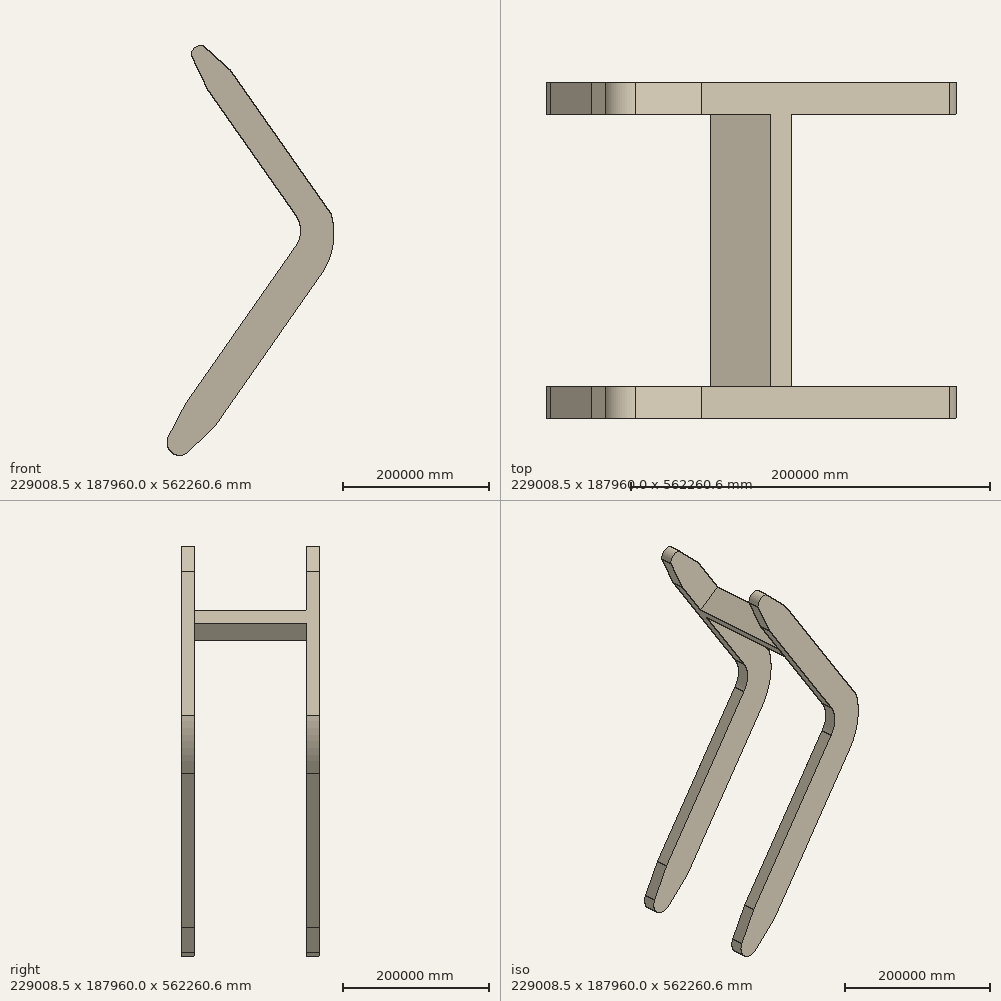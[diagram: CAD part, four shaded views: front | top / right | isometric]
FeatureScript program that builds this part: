
annotation { "Feature Type Name" : "Feature", "Feature Type Description" : "" }
export const myFeature = defineFeature(function(context is Context, id is Id, definition is map)
    precondition{}
    {
        {
            var Q0;
            Q0=qCreatedBy(makeId("Front.planeOp"),FACE);
            var sketch = newSketch(context, id + "F0", { "sketchPlane" : qUnion([Q0])});
            skLineSegment(sketch, "E0", {"start": v(-106253.88, 96824.48) * mm, "end": v(-45990.24, 10942.25) * mm});
            skArc(sketch, "E1", {"start": v(-27263.76, -28488.04) * mm, "mid": v(-20134.7, -9159.77) * mm, "end": v(-21485.77, 11396.98) * mm});
            skLineSegment(sketch, "E2", {"start": v(-21485.77, 11396.98) * mm, "end": v(-90790.44, 110163.66) * mm});
            skLineSegment(sketch, "E3", {"start": v(-45968.36, -10911) * mm, "end": v(-121497.82, -119008.48) * mm});
            skLineSegment(sketch, "E4", {"start": v(-27263.76, -28488.04) * mm, "end": v(-101187.58, -134287.53) * mm});
            skLineSegment(sketch, "E5", {"start": v(-101187.58, -134287.53) * mm, "end": v(-119329.15, -151628.38) * mm});
            skLineSegment(sketch, "E6", {"start": v(-121497.82, -119008.48) * mm, "end": v(-133130.37, -141245.96) * mm});
            skArc(sketch, "E7", {"start": v(-133130.37, -141245.96) * mm, "mid": v(-130636.96, -152295.6) * mm, "end": v(-119329.15, -151628.38) * mm});
            skLineSegment(sketch, "E8", {"start": v(-90790.44, 110163.66) * mm, "end": v(-109391.03, 127010.27) * mm});
            skLineSegment(sketch, "E9", {"start": v(-106253.88, 96824.48) * mm, "end": v(-117539.26, 120505.01) * mm});
            skArc(sketch, "E10", {"start": v(-109391.03, 127010.27) * mm, "mid": v(-114859.1, 125503.66) * mm, "end": v(-117539.26, 120505.01) * mm});
            skArc(sketch, "E11.filletArc", {"start": v(-45968.36, -10911) * mm, "mid": v(-42534.15, 19.08) * mm, "end": v(-45990.24, 10942.25) * mm});
            skSolve(sketch);
        }
        {
            var Q0;
            Q0 = qSketchRegion(id + "F0", true);
            extrude(context, id + "F1", {"entities" : qUnion([Q0]), "depth" : 8890 * mm, "offsetDistance" : 25.4 * mm});
        }
        {
            var Q0;
            Q0=makeQuery(id+"F1.opExtrude","CAP_FACE",FACE,{"disambiguationData":[OSD([sQuery(id+"F0.wireOp",EDGE,"E0"),sQuery(id+"F0.wireOp",EDGE,"E1"),sQuery(id+"F0.wireOp",EDGE,"E2"),sQuery(id+"F0.wireOp",EDGE,"E3"),sQuery(id+"F0.wireOp",EDGE,"E4"),sQuery(id+"F0.wireOp",EDGE,"E5"),sQuery(id+"F0.wireOp",EDGE,"E6"),sQuery(id+"F0.wireOp",EDGE,"E7"),sQuery(id+"F0.wireOp",EDGE,"E8"),sQuery(id+"F0.wireOp",EDGE,"E9"),sQuery(id+"F0.wireOp",EDGE,"E10"),sQuery(id+"F0.wireOp",EDGE,"E11.filletArc")])],"isStart":true});
            cPlane(context, id + "F2", {"entities" : qUnion([Q0]), "cplaneType" : CPlaneType.OFFSET, "offset" : 25.4 * mm, "width" : 152.4 * mm, "height" : 152.4 * mm});
        }
        {
            var Q0;
            Q0=qCreatedBy(id+"F2.planeOp",FACE);
            var sketch = newSketch(context, id + "F3", { "sketchPlane" : qUnion([Q0])});
            skLineSegment(sketch, "E12.0", {"start": v(106253.88, 96824.48) * mm, "end": v(45990.24, 10942.25) * mm});
            skLineSegment(sketch, "E12.1", {"start": v(21485.77, 11396.98) * mm, "end": v(90790.44, 110163.66) * mm});
            skLineSegment(sketch, "E13", {"start": v(82464.42, 62921.9) * mm, "end": v(65830.93, 74593.64) * mm});
            skLineSegment(sketch, "E14", {"start": v(88300.28, 71238.65) * mm, "end": v(71666.8, 82910.39) * mm});
            skSolve(sketch);
        }
        {
            var Q0;
            Q0 = qSketchRegion(id + "F3", true);
            extrude(context, id + "F4", {"entities" : qUnion([Q0]), "depth" : 76200 * mm, "offsetDistance" : 25.4 * mm});
        }
        {
            var Q0;
            Q0=makeQuery(id+"F1.opExtrude","CAP_FACE",FACE,{"disambiguationData":[OSD([sQuery(id+"F0.wireOp",EDGE,"E0"),sQuery(id+"F0.wireOp",EDGE,"E1"),sQuery(id+"F0.wireOp",EDGE,"E2"),sQuery(id+"F0.wireOp",EDGE,"E3"),sQuery(id+"F0.wireOp",EDGE,"E4"),sQuery(id+"F0.wireOp",EDGE,"E5"),sQuery(id+"F0.wireOp",EDGE,"E6"),sQuery(id+"F0.wireOp",EDGE,"E7"),sQuery(id+"F0.wireOp",EDGE,"E8"),sQuery(id+"F0.wireOp",EDGE,"E9"),sQuery(id+"F0.wireOp",EDGE,"E10"),sQuery(id+"F0.wireOp",EDGE,"E11.filletArc")])],"isStart":true});
            cPlane(context, id + "F5", {"entities" : qUnion([Q0]), "cplaneType" : CPlaneType.OFFSET, "offset" : 38100 * mm, "width" : 152.4 * mm, "height" : 152.4 * mm});
        }
        {
            var Q0;
            Q0=makeQuery(id+"F1.opExtrude","SWEPT_BODY",BODY,{"disambiguationData":[OSD([sQuery(id+"F0.wireOp",EDGE,"E0"),sQuery(id+"F0.wireOp",EDGE,"E1"),sQuery(id+"F0.wireOp",EDGE,"E2"),sQuery(id+"F0.wireOp",EDGE,"E3"),sQuery(id+"F0.wireOp",EDGE,"E4"),sQuery(id+"F0.wireOp",EDGE,"E5"),sQuery(id+"F0.wireOp",EDGE,"E6"),sQuery(id+"F0.wireOp",EDGE,"E7"),sQuery(id+"F0.wireOp",EDGE,"E8"),sQuery(id+"F0.wireOp",EDGE,"E9"),sQuery(id+"F0.wireOp",EDGE,"E10"),sQuery(id+"F0.wireOp",EDGE,"E11.filletArc")])]});
            var Q1;
            Q1=qCreatedBy(id+"F5.planeOp",FACE);
            mirror(context, id + "F6", {"operationType" : NewBodyOperationType.ADD, "entities" : qUnion([Q0]), "mirrorPlane" : qUnion([Q1])});
        }
        {
            var Q0;
            Q0=makeQuery(id+"F4.opExtrude","SWEPT_BODY",BODY,{"disambiguationData":[OSD([sQuery(id+"F3.wireOp",EDGE,"E12.0"),sQuery(id+"F3.wireOp",EDGE,"E12.1"),sQuery(id+"F3.wireOp",EDGE,"E13"),sQuery(id+"F3.wireOp",EDGE,"E14")])]});
            var Q1;
            Q1=makeQuery(id+"F1.opExtrude","SWEPT_BODY",BODY,{"disambiguationData":[OSD([sQuery(id+"F0.wireOp",EDGE,"E0"),sQuery(id+"F0.wireOp",EDGE,"E1"),sQuery(id+"F0.wireOp",EDGE,"E2"),sQuery(id+"F0.wireOp",EDGE,"E3"),sQuery(id+"F0.wireOp",EDGE,"E4"),sQuery(id+"F0.wireOp",EDGE,"E5"),sQuery(id+"F0.wireOp",EDGE,"E6"),sQuery(id+"F0.wireOp",EDGE,"E7"),sQuery(id+"F0.wireOp",EDGE,"E8"),sQuery(id+"F0.wireOp",EDGE,"E9"),sQuery(id+"F0.wireOp",EDGE,"E10"),sQuery(id+"F0.wireOp",EDGE,"E11.filletArc")])]});
            var Q2;
            Q2=makeQuery(id+"F1.opExtrude","CAP_VERTEX",VERTEX,{"disambiguationData":[OSD([sQuery(id+"F0.wireOp",EDGE,"E2"),sQuery(id+"F0.wireOp",EDGE,"E8")])],"isStart":true});
            transform(context, id + "F7", {"entities" : qUnion([Q0, Q1]), "transformType" : TransformType.SCALE_UNIFORMLY, "scale" : 2, "scalePoint" : qUnion([Q2]), "makeCopy" : false});
        }
    });
